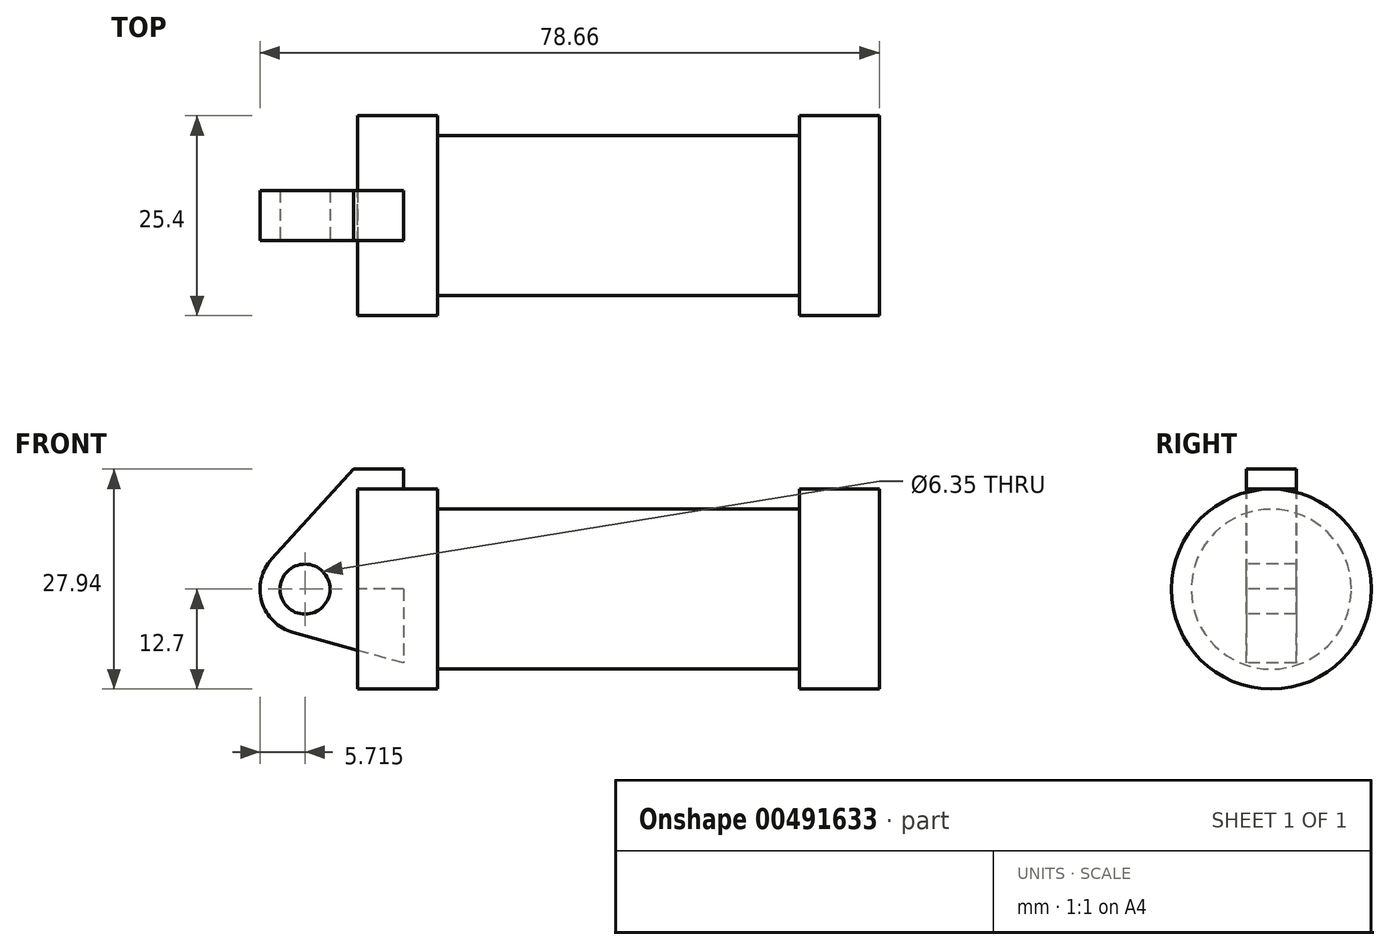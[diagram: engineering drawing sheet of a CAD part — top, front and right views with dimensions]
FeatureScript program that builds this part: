
annotation { "Feature Type Name" : "Feature", "Feature Type Description" : "" }
export const myFeature = defineFeature(function(context is Context, id is Id, definition is map)
    precondition{}
    {
        {
            var Q0;
            Q0=qCreatedBy(makeId("Front.planeOp"),FACE);
            var sketch = newSketch(context, id + "F0", { "sketchPlane" : qUnion([Q0])});
            skLineSegment(sketch, "E0", {"start": v(0, 0) * mm, "end": v(0, 12.7) * mm});
            skLineSegment(sketch, "E1", {"start": v(0, 12.7) * mm, "end": v(10.16, 12.7) * mm});
            skLineSegment(sketch, "E2", {"start": v(10.16, 12.7) * mm, "end": v(10.16, 10.16) * mm});
            skLineSegment(sketch, "E3", {"start": v(10.16, 10.16) * mm, "end": v(56.13, 10.16) * mm});
            skLineSegment(sketch, "E4", {"start": v(56.13, 10.16) * mm, "end": v(56.13, 12.7) * mm});
            skLineSegment(sketch, "E5", {"start": v(56.13, 12.7) * mm, "end": v(66.3, 12.7) * mm});
            skLineSegment(sketch, "E6", {"start": v(66.3, 12.7) * mm, "end": v(66.3, 0) * mm});
            skLineSegment(sketch, "E7", {"start": v(66.3, 0) * mm, "end": v(0, 0) * mm});
            skLineSegment(sketch, "E8", {"start": v(5.84, 15.24) * mm, "end": v(-0.5, 15.24) * mm});
            skLineSegment(sketch, "E9", {"start": v(-0.5, 15.24) * mm, "end": v(-10.88, 3.85) * mm});
            skLineSegment(sketch, "E10", {"start": v(0, 0) * mm, "end": v(-6.65, 0) * mm});
            skCircle(sketch, "E11", {"center": v(-6.65, 0) * mm, "radius": 5.72 * mm});
            skCircle(sketch, "E12", {"center": v(-6.65, 0) * mm, "radius": 3.18 * mm});
            skLineSegment(sketch, "E13", {"start": v(5.84, 15.24) * mm, "end": v(5.84, -9.4) * mm});
            skLineSegment(sketch, "E14", {"start": v(5.84, -9.4) * mm, "end": v(-8.18, -5.5) * mm});
            skSolve(sketch);
        }
        {
            var Q0;
            {var subQ0=sQuery(id+"F0.wireOp",EDGE,"E2");Q0=makeQuery(id+"F0.imprint","IMPRINT",FACE,{"disambiguationData":[TD([[makeQuery(id+"F0.imprint","IMPRINT",EDGE,{"derivedFrom":subQ0}),-1.0]])]});}
            var Q1;
            {var subQ0=sQuery(id+"F0.wireOp",EDGE,"E0");Q1=makeQuery(id+"F0.imprint","IMPRINT",FACE,{"disambiguationData":[TD([[makeQuery(id+"F0.imprint","IMPRINT",EDGE,{"derivedFrom":subQ0}),-1.0]])]});}
            var Q2;
            Q2=sQuery(id+"F0.wireOp",EDGE,"E7");
            revolve(context, id + "F1", {"entities" : qUnion([Q0, Q1]), "axis" : qUnion([Q2]), "revolveType" : RevolveType.FULL});
        }
        {
            var Q0;
            {var subQ0=sQuery(id+"F0.wireOp",EDGE,"E14");Q0=makeQuery(id+"F0.imprint","IMPRINT",FACE,{"disambiguationData":[TD([[makeQuery(id+"F0.imprint","IMPRINT",EDGE,{"derivedFrom":subQ0}),-1.0]])]});}
            var Q1;
            {var subQ1=sQuery(id+"F0.wireOp",EDGE,"E0");Q1=makeQuery(id+"F0.imprint","IMPRINT",FACE,{"disambiguationData":[TD([[makeQuery(id+"F0.imprint","IMPRINT",EDGE,{"derivedFrom":subQ1}),1.0]])]});}
            var Q2;
            {var subQ5=sQuery(id+"F0.wireOp",EDGE,"E12");Q2=makeQuery(id+"F0.imprint","IMPRINT",FACE,{"disambiguationData":[TD([[makeQuery(id+"F0.imprint","IMPRINT",EDGE,{"derivedFrom":subQ5}),-1.0]])]});}
            extrude(context, id + "F2", {"entities" : qUnion([Q0, Q1, Q2]), "endBound" : BoundingType.SYMMETRIC, "oppositeDirection" : true, "depth" : 6.35 * mm});
        }
    });
